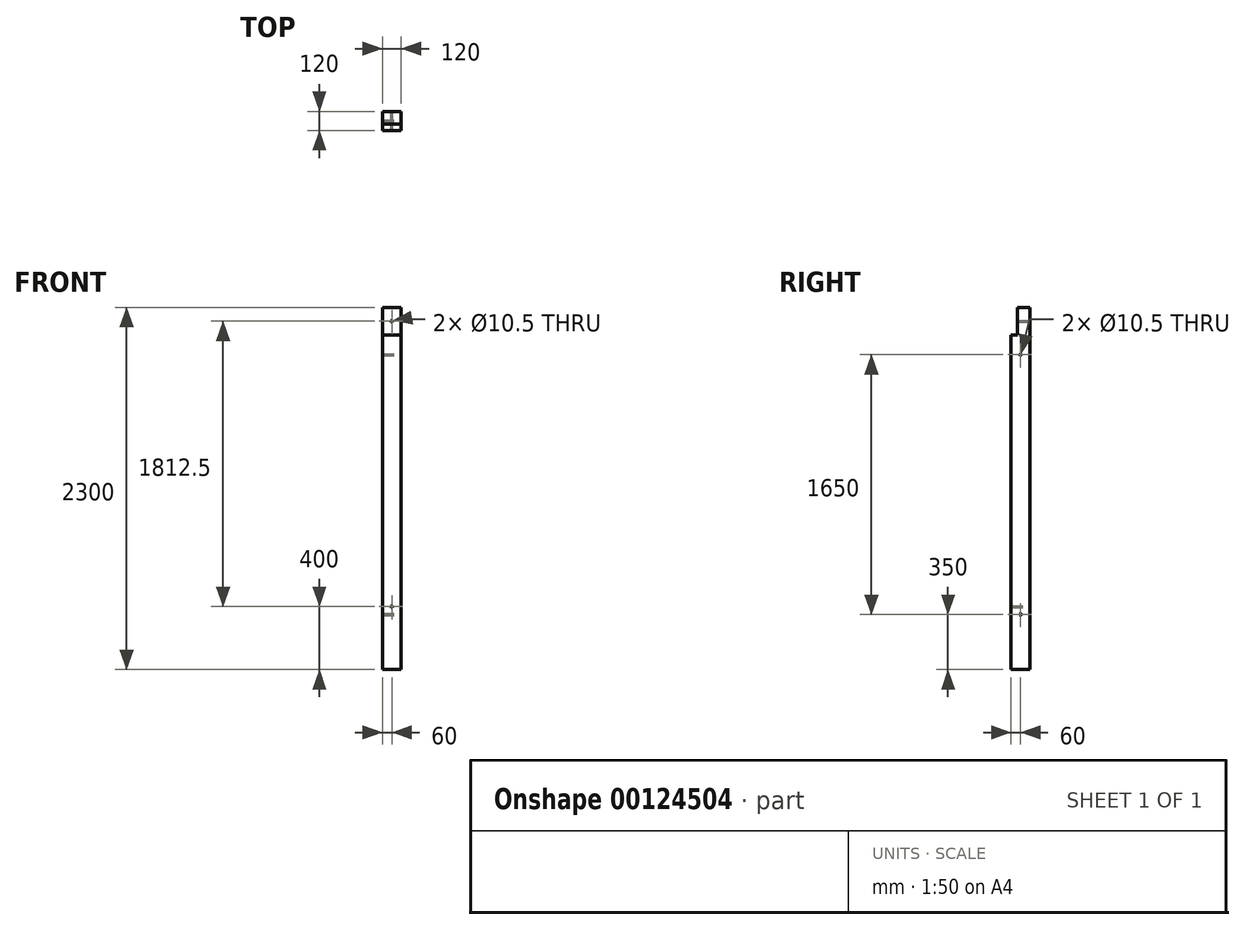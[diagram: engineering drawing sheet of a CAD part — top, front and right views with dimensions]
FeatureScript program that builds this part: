
annotation { "Feature Type Name" : "Feature", "Feature Type Description" : "" }
export const myFeature = defineFeature(function(context is Context, id is Id, definition is map)
    precondition{}
    {
        {
            var Q0;
            Q0=qCreatedBy(makeId("Top.planeOp"),FACE);
            var sketch = newSketch(context, id + "F0", { "sketchPlane" : qUnion([Q0])});
            skLineSegment(sketch, "E0", {"start": v(0, 0) * mm, "end": v(0, 330.83) * mm, "construction": true});
            skLineSegment(sketch, "E1", {"start": v(-296.67, 0) * mm, "end": v(360, 0) * mm, "construction": true});
            skLineSegment(sketch, "E2.bottom", {"start": v(60, 60) * mm, "end": v(-60, 60) * mm});
            skLineSegment(sketch, "E2.top", {"start": v(60, -60) * mm, "end": v(-60, -60) * mm});
            skLineSegment(sketch, "E2.left", {"start": v(60, 60) * mm, "end": v(60, -60) * mm});
            skLineSegment(sketch, "E2.right", {"start": v(-60, 60) * mm, "end": v(-60, -60) * mm});
            skPoint(sketch, "E2.middle", {"position": v(0, 0) * mm});
            skPoint(sketch, "E3.visualSharp", {"position": v(-60, 60) * mm});
            skPoint(sketch, "E4.visualSharp", {"position": v(60, 60) * mm});
            skPoint(sketch, "E5.visualSharp", {"position": v(-60, -60) * mm});
            skPoint(sketch, "E6.visualSharp", {"position": v(60, -60) * mm});
            skSolve(sketch);
        }
        {
            var Q0;
            Q0=qSketchRegion(id+"F0",true);
            extrude(context, id + "F1", {"entities" : qUnion([Q0]), "endBound" : BoundingType.SYMMETRIC, "depth" : 2300 * mm});
        }
        {
            var Q0;
            Q0=makeQuery(id+"F1.opExtrude","SWEPT_FACE",FACE,{"disambiguationData":[OSD([sQuery(id+"F0.wireOp",EDGE,"E2.left")])]});
            var sketch = newSketch(context, id + "F2", { "sketchPlane" : qUnion([Q0])});
            skLineSegment(sketch, "E7.bottom", {"start": v(-60, 1150) * mm, "end": v(-20, 1150) * mm});
            skLineSegment(sketch, "E7.top", {"start": v(-60, 975) * mm, "end": v(-20, 975) * mm});
            skLineSegment(sketch, "E7.left", {"start": v(-60, 1150) * mm, "end": v(-60, 975) * mm});
            skLineSegment(sketch, "E7.right", {"start": v(-20, 1150) * mm, "end": v(-20, 975) * mm});
            skSolve(sketch);
        }
        {
            var Q0;
            Q0=qSketchRegion(id+"F2",true);
            extrude(context, id + "F3", {"entities" : qUnion([Q0]), "operationType" : NewBodyOperationType.REMOVE, "endBound" : BoundingType.UP_TO_NEXT, "oppositeDirection" : true, "depth" : 25 * mm});
        }
        {
            var Q0;
            Q0=makeQuery(id+"F1.opExtrude","SWEPT_FACE",FACE,{"disambiguationData":[OSD([sQuery(id+"F0.wireOp",EDGE,"E2.bottom")])]});
            var sketch = newSketch(context, id + "F4", { "sketchPlane" : qUnion([Q0])});
            skCircle(sketch, "E8", {"center": v(0, 1062.5) * mm, "radius": 5.25 * mm});
            skCircle(sketch, "E9", {"center": v(0, -750) * mm, "radius": 5.25 * mm});
            skSolve(sketch);
        }
        {
            var Q0;
            Q0 = qSketchRegion(id + "F4", true);
            extrude(context, id + "F5", {"entities" : qUnion([Q0]), "operationType" : NewBodyOperationType.REMOVE, "endBound" : BoundingType.THROUGH_ALL, "oppositeDirection" : true, "depth" : 25 * mm});
        }
        {
            var Q0;
            Q0=makeQuery(id+"F1.opExtrude","SWEPT_FACE",FACE,{"disambiguationData":[OSD([sQuery(id+"F0.wireOp",EDGE,"E2.left")])]});
            var sketch = newSketch(context, id + "F6", { "sketchPlane" : qUnion([Q0])});
            skCircle(sketch, "E10", {"center": v(0, -800) * mm, "radius": 5.25 * mm});
            skCircle(sketch, "E11", {"center": v(0, 850) * mm, "radius": 5.25 * mm});
            skSolve(sketch);
        }
        {
            var Q0;
            Q0 = qSketchRegion(id + "F6", true);
            extrude(context, id + "F7", {"entities" : qUnion([Q0]), "operationType" : NewBodyOperationType.REMOVE, "endBound" : BoundingType.THROUGH_ALL, "oppositeDirection" : true, "depth" : 25 * mm});
        }
    });
